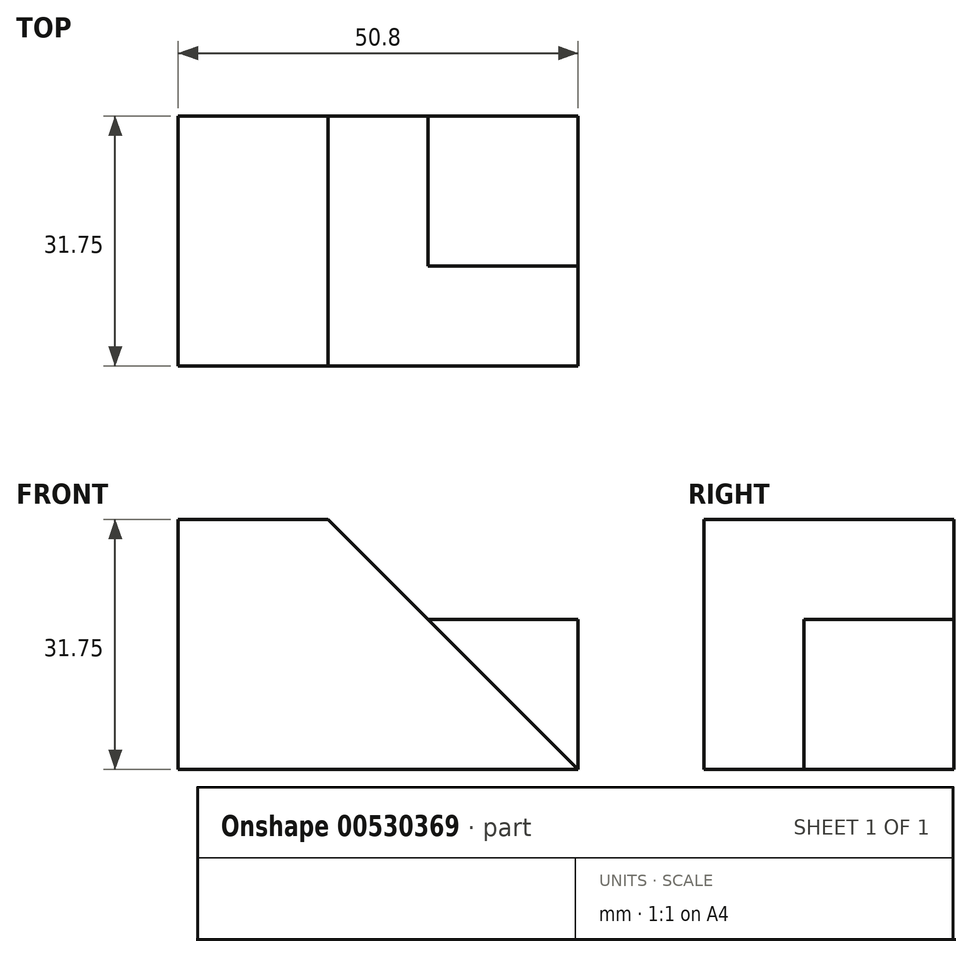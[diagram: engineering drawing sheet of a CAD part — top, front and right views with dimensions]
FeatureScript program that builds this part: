
annotation { "Feature Type Name" : "Feature", "Feature Type Description" : "" }
export const myFeature = defineFeature(function(context is Context, id is Id, definition is map)
    precondition{}
    {
        {
            var Q0;
            Q0=qCreatedBy(makeId("Front.planeOp"),FACE);
            var sketch = newSketch(context, id + "F0", { "sketchPlane" : qUnion([Q0])});
            skLineSegment(sketch, "E0", {"start": v(-50.8, 31.75) * mm, "end": v(-50.8, 0) * mm});
            skLineSegment(sketch, "E1", {"start": v(-50.8, 0) * mm, "end": v(0, 0) * mm});
            skLineSegment(sketch, "E2", {"start": v(-50.8, 31.75) * mm, "end": v(-31.75, 31.75) * mm});
            skLineSegment(sketch, "E3", {"start": v(-31.75, 31.75) * mm, "end": v(0, 0) * mm});
            skSolve(sketch);
        }
        {
            var Q0;
            Q0=makeQuery(id+"F0.imprint","IMPRINT",FACE,{"disambiguationData":[TD([[makeQuery(id+"F0.imprint","IMPRINT",EDGE,{"derivedFrom":sQuery(id+"F0.wireOp",EDGE,"E0")}),1.0]])]});
            extrude(context, id + "F1", {"entities" : qUnion([Q0]), "depth" : 31.75 * mm, "offsetDistance" : 25.4 * mm});
        }
        {
            var Q0;
            Q0=qCreatedBy(makeId("Front.planeOp"),FACE);
            var sketch = newSketch(context, id + "F2", { "sketchPlane" : qUnion([Q0])});
            skLineSegment(sketch, "E4", {"start": v(0, 0) * mm, "end": v(0, 19.05) * mm});
            skLineSegment(sketch, "E5", {"start": v(0, 19.05) * mm, "end": v(-19.05, 19.05) * mm});
            skLineSegment(sketch, "E6", {"start": v(-19.05, 19.05) * mm, "end": v(0, 0) * mm});
            skSolve(sketch);
        }
        {
            var Q0;
            Q0=makeQuery(id+"F2.imprint","IMPRINT",FACE,{"disambiguationData":[TD([[makeQuery(id+"F2.imprint","IMPRINT",EDGE,{"derivedFrom":sQuery(id+"F2.wireOp",EDGE,"E4")}),1.0]])]});
            extrude(context, id + "F3", {"entities" : qUnion([Q0]), "operationType" : NewBodyOperationType.ADD, "depth" : 19.05 * mm, "offsetDistance" : 25.4 * mm});
        }
    });
